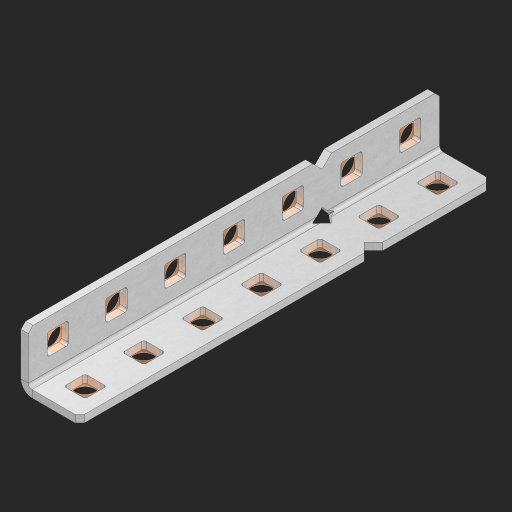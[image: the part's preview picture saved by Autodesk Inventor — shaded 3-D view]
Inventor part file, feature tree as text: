
AUTODESK INVENTOR PART (.ipt)
format: ipt  version: 2023 (Build 270158000, 158)  size: 550,400 bytes
history: native  units: in
note: dims shown in document units (in); Inventor stores cm internally (conversion verified against a paired STEP export)
features: other x20, extrude x15, sheet_metal_op x8, sketch x5, pattern_linear x1, mirror x1, chamfer x1
ambient origin geometry x8: Origin, YZ Plane, XZ Plane, XY Plane, X Axis, Y Axis, Z Axis, Center Point
bodies: Solid1 (feature_tree), Body (feature_tree)
feature tree (51):
  sheet_metal_op  "Flanges"
  sheet_metal_op  "Body Pattern"
  other  "Arc Length"
  pattern_linear  "Notch Pattern"  Spacing1=0.125in  [1 undecoded]
  other  "Diagonal Plane"
  mirror  "Everything Mirrored"
  chamfer  "End Chamfer"
  sketch  "Sketch1"  dims[d0=0.5in]
  other  "Plate1"
  sketch  "Sketch2"  dims[d1=3.5in]
  other  "Plate2"
  sheet_metal_op  "Bend1"
  sheet_metal_op  "Corner1"
  sketch  "Sketch8"  dims[d2=0.0625in]
  sketch  "Sketch9"  dims[d3=0.0625in]
  other  "Srf91"
  sheet_metal_op  "Body Pattern Sketch"
  other  "Srf92"
  sketch  "Sketch13"  dims[d4=0.0312in d5=0.125in d6=0.0625in d7=0.5in d8=90.0deg d9=0.0312in d10=0.25in d11=0.0625in d12=0.0625in d49=0.182in d50=0.02in d52=0.25in d53=0.0625in d54=0.0in d55=0.172in d56=1.0in d57=0.0in d85=0.1473in d86=0.1782in d89=0.0625in d90=0.0in d91=0.04in d92=0.0491in d95=2.5in d96=0.04in d97=0.25in d98=45.0deg d123=0.204in d126=0.0491in d127=0.1473in d128=0.08in d129=0.04in d130=2.5in d131=2.7559in d133=0.5in d134=0.3937in d136=1.0in]
  other  "Srf856"
  other  "Srf857"
  other  "Srf858"
  other  "Srf859"
  other  "Srf860"
  other  "Srf861"
  other  "Srf1275"
  other  "Srf1276"
  other  "Srf1278"
  other  "Srf1279"
  other  "Srf1280"
  other  "Srf1281"
  other  "Srf1282"
  other  "Srf1283"
  sheet_metal_op  "Body Stamp"
  sheet_metal_op  "Body Circle"
  sheet_metal_op  "Notch"
  extrude  "ExtrusionSrf92"  Depth=0.0625in
  extrude  "ExtrusionSrf856"  Depth=0.5in TaperAngle=90.0deg
  extrude  "ExtrusionSrf857"  Depth=0.3937in
  extrude  "ExtrusionSrf858"  Depth=0.0625in
  extrude  "ExtrusionSrf859"  Depth=0.0625in
  extrude  "ExtrusionSrf860"  Depth=0.3937in
  extrude  "ExtrusionSrf861"  Depth=0.02in
  extrude  "ExtrusionSrf1275"  Depth=0.3937in
  extrude  "ExtrusionSrf1276"  Depth=0.0625in
  extrude  "ExtrusionSrf1277"  TaperAngle=0.0deg  [1 undecoded]
  extrude  "ExtrusionSrf1278"  Depth=0.3937in
  extrude  "ExtrusionSrf1279"  Depth=0.3937in TaperAngle=0.0deg
  extrude  "ExtrusionSrf1280"  Depth=0.3937in
  extrude  "ExtrusionSrf1281"  Depth=0.3937in
  extrude  "ExtrusionSrf1282"  Depth=0.0625in
note: 2 required parameter values undecoded (feature->parameter linkage not recoverable at this tier; creation-order binding heuristic only, values carry confidence <= 0.55)
